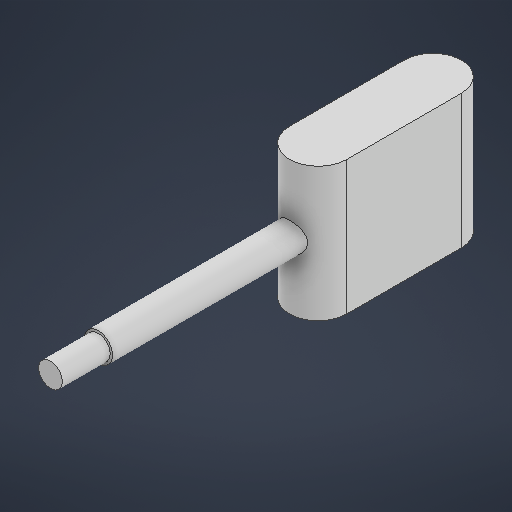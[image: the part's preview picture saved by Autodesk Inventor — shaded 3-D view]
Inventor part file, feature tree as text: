
AUTODESK INVENTOR PART (.ipt)
format: ipt  version: 2025.3 (Build 293356000, 356)  size: 211,456 bytes
history: native  units: mm
features: extrude x3, sketch x3, plane x1
ambient origin geometry x8: Origin, YZ Plane, XZ Plane, XY Plane, X Axis, Y Axis, Z Axis, Center Point
bodies: Solid1 (feature_tree)
feature tree (7):
  extrude  "Extrusion1"  Depth=3.0mm
  plane  "Work Plane1"
  extrude  "Extrusion2"  Depth=14.0mm TaperAngle=0.0deg
  extrude  "Extrusion3"  Depth=5.0mm
  sketch  "Sketch1"  dims[d0=12.0mm d1=3.0mm]
  sketch  "Sketch2"  dims[d2=20.0mm d3=14.0mm d4=0.0mm]
  sketch  "Sketch3"  dims[d5=3.0mm d6=7.0mm d7=3.0mm d8=25.0mm d9=2.0mm d10=0.0mm d11=0.0mm d12=2.5mm d13=5.0mm d14=0.0mm]
